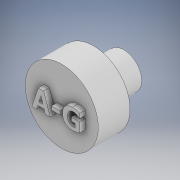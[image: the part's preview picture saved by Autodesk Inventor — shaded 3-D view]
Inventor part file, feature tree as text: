
AUTODESK INVENTOR PART (.ipt)
format: ipt  version: 2022 (Build 260153000, 153)  size: 172,544 bytes
history: native  units: in
note: dims shown in document units (in); Inventor stores cm internally (conversion verified against a paired STEP export)
features: sketch x3, extrude x3
ambient origin geometry x8: Origin, YZ Plane, XZ Plane, XY Plane, X Axis, Y Axis, Z Axis, Center Point
bodies: Solid1 (feature_tree)
feature tree (6):
  sketch  "Sketch1"  dims[d0=0.4898in d1=0.0185in]
  extrude  "Extrusion1"  Depth=0.0185in
  extrude  "Extrusion2"  Depth=0.1969in TaperAngle=0.0deg
  sketch  "Sketch2"  dims[d2=0.1969in d3=0.0in d4=0.189in d5=0.0in]
  extrude  "Extrusion7"  [1 undecoded]
  sketch  "Sketch3"  dims[d14=0.0354in d15=0.0in]
note: 1 required parameter value undecoded (feature->parameter linkage not recoverable at this tier; creation-order binding heuristic only, values carry confidence <= 0.55)
